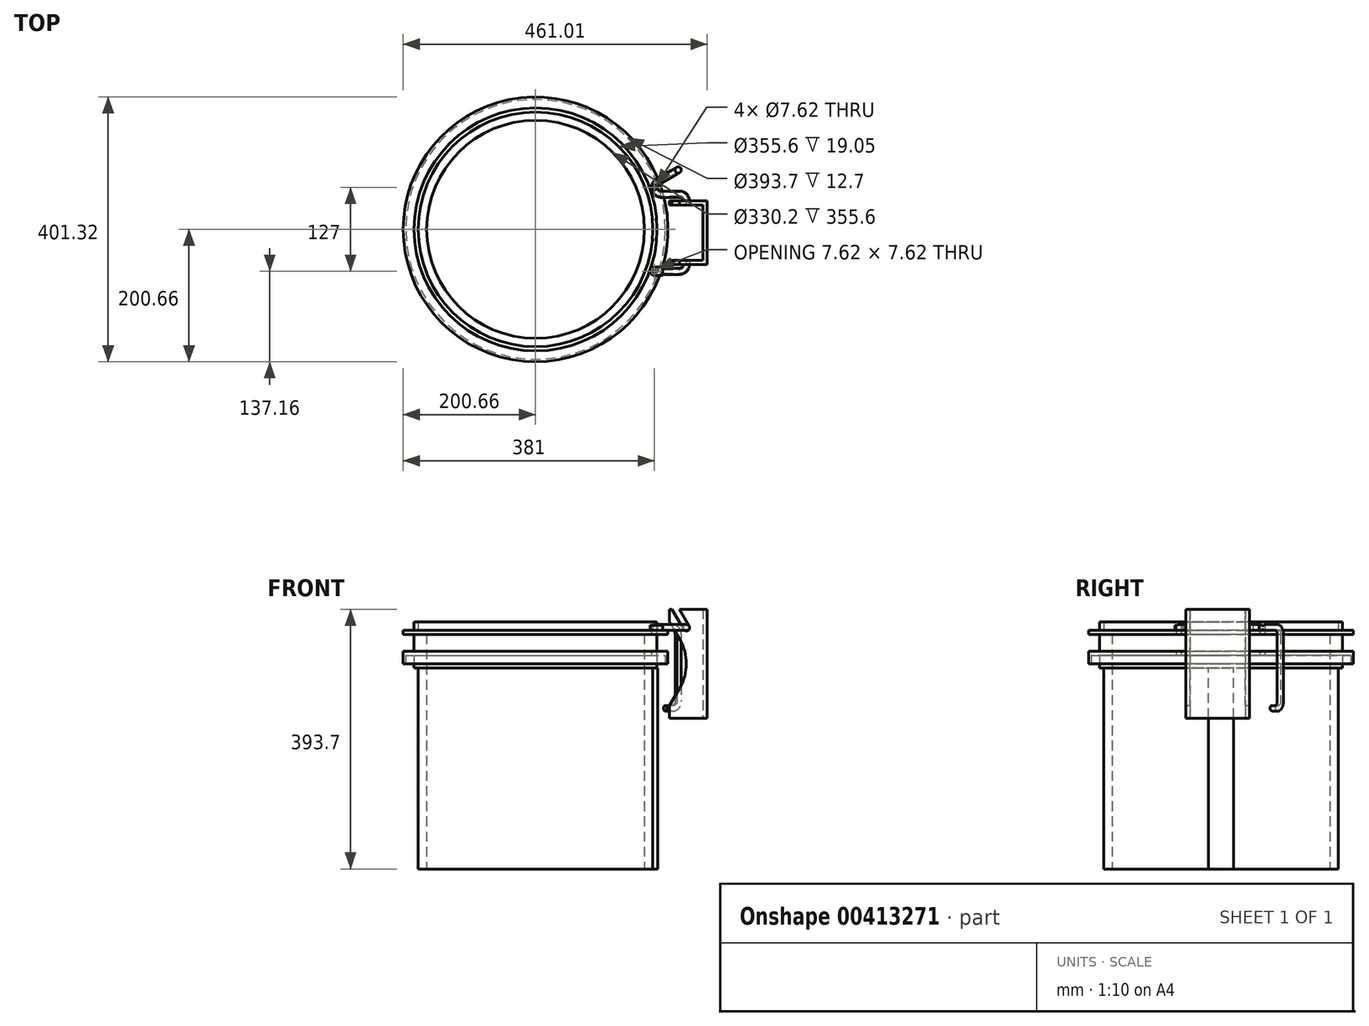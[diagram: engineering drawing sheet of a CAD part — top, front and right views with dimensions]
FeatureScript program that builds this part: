
annotation { "Feature Type Name" : "Feature", "Feature Type Description" : "" }
export const myFeature = defineFeature(function(context is Context, id is Id, definition is map)
    precondition{}
    {
        {
            var Q0;
            Q0=qCreatedBy(makeId("Front.planeOp"),FACE);
            var sketch = newSketch(context, id + "F0", { "sketchPlane" : qUnion([Q0])});
            skLineSegment(sketch, "E0", {"start": v(0, 0) * mm, "end": v(6.35, 0) * mm});
            skLineSegment(sketch, "E1", {"start": v(6.35, 0) * mm, "end": v(6.35, 19.05) * mm});
            skLineSegment(sketch, "E2", {"start": v(6.35, 19.05) * mm, "end": v(19.05, 19.05) * mm});
            skLineSegment(sketch, "E3", {"start": v(19.05, 19.05) * mm, "end": v(19.05, 6.35) * mm});
            skLineSegment(sketch, "E4", {"start": v(19.05, 6.35) * mm, "end": v(22.86, 6.35) * mm});
            skLineSegment(sketch, "E5", {"start": v(22.86, 6.35) * mm, "end": v(22.86, 25.4) * mm});
            skLineSegment(sketch, "E6", {"start": v(22.86, 25.4) * mm, "end": v(6.35, 25.4) * mm});
            skLineSegment(sketch, "E7", {"start": v(0, 25.4) * mm, "end": v(0, 0) * mm});
            skLineSegment(sketch, "E8", {"start": v(6.35, 25.4) * mm, "end": v(6.35, 50.8) * mm});
            skLineSegment(sketch, "E9", {"start": v(0, 50.8) * mm, "end": v(0, 25.4) * mm});
            skPoint(sketch, "E10", {"position": v(6.35, 25.4) * mm});
            skLineSegment(sketch, "E11", {"start": v(-177.8, 9.24) * mm, "end": v(-177.8, 50.6) * mm, "construction": true});
            skLineSegment(sketch, "E12", {"start": v(6.35, 50.8) * mm, "end": v(22.86, 50.8) * mm});
            skLineSegment(sketch, "E13", {"start": v(22.86, 50.8) * mm, "end": v(22.86, 57.15) * mm});
            skLineSegment(sketch, "E14", {"start": v(22.86, 57.15) * mm, "end": v(6.35, 57.15) * mm});
            skLineSegment(sketch, "E15", {"start": v(6.35, 57.15) * mm, "end": v(6.35, 69.85) * mm});
            skLineSegment(sketch, "E16", {"start": v(6.35, 69.85) * mm, "end": v(0, 69.85) * mm});
            skLineSegment(sketch, "E17", {"start": v(0, 69.85) * mm, "end": v(0, 50.8) * mm});
            skSolve(sketch);
        }
        {
            var Q0;
            Q0 = qSketchRegion(id + "F0", true);
            var Q1;
            Q1=sQuery(id+"F0.wireOp",EDGE,"E11");
            revolve(context, id + "F1", {"entities" : qUnion([Q0]), "axis" : qUnion([Q1]), "revolveType" : RevolveType.FULL});
        }
        {
            var Q0;
            Q0=makeQuery(id+"F1.opRevolve","SWEPT_FACE",FACE,{"disambiguationData":[OSD([sQuery(id+"F0.wireOp",EDGE,"E14")])]});
            var sketch = newSketch(context, id + "F2", { "sketchPlane" : qUnion([Q0])});
            skLineSegment(sketch, "E18", {"start": v(2.54, -87.99) * mm, "end": v(2.54, 87.99) * mm, "construction": true});
            skLineSegment(sketch, "E19", {"start": v(2.54, 0) * mm, "end": v(22.86, 0) * mm, "construction": true});
            skCircle(sketch, "E20", {"center": v(2.54, -63.5) * mm, "radius": 3.81 * mm});
            skCircle(sketch, "E21.MirrorC", {"center": v(2.54, 63.5) * mm, "radius": 3.81 * mm});
            skSolve(sketch);
        }
        {
            var Q0;
            Q0 = qSketchRegion(id + "F2", true);
            extrude(context, id + "F3", {"entities" : qUnion([Q0]), "operationType" : NewBodyOperationType.REMOVE, "endBound" : BoundingType.THROUGH_ALL, "oppositeDirection" : true, "depth" : 25.4 * mm});
        }
        {
            var Q0;
            Q0=makeQuery(id+"F1.opRevolve","SWEPT_FACE",FACE,{"disambiguationData":[OSD([sQuery(id+"F0.wireOp",EDGE,"E14")])]});
            var sketch = newSketch(context, id + "F4", { "sketchPlane" : qUnion([Q0])});
            skCircle(sketch, "E22", {"center": v(2.54, -63.5) * mm, "radius": 3.8 * mm});
            skLineSegment(sketch, "E23", {"start": v(2.54, -63.5) * mm, "end": v(27.94, -63.5) * mm, "construction": true});
            skLineSegment(sketch, "E24", {"start": v(15.24, -57.15) * mm, "end": v(2.54, -57.15) * mm});
            skPoint(sketch, "E24.startSnap0", {"position": v(15.24, -63.5) * mm});
            skLineSegment(sketch, "E25", {"start": v(2.54, -57.15) * mm, "end": v(2.54, -63.5) * mm, "construction": true});
            skArc(sketch, "E26", {"start": v(2.54, -57.15) * mm, "mid": v(-3.81, -63.5) * mm, "end": v(2.54, -69.85) * mm});
            skLineSegment(sketch, "E27", {"start": v(2.54, -69.85) * mm, "end": v(15.24, -69.85) * mm});
            skLineSegment(sketch, "E28", {"start": v(15.24, -69.85) * mm, "end": v(15.24, -57.15) * mm});
            skSolve(sketch);
        }
        {
            var Q0;
            Q0 = qSketchRegion(id + "F4", true);
            extrude(context, id + "F5", {"entities" : qUnion([Q0]), "depth" : 7.62 * mm});
        }
        {
            var Q0;
            Q0=makeQuery(id+"F5.opExtrude","SWEPT_FACE",FACE,{"disambiguationData":[OSD([sQuery(id+"F4.wireOp",EDGE,"E28")])]});
            var sketch = newSketch(context, id + "F6", { "sketchPlane" : qUnion([Q0])});
            skLineSegment(sketch, "E29", {"start": v(-69.85, 60.96) * mm, "end": v(-57.15, 60.96) * mm, "construction": true});
            skCircle(sketch, "E30", {"center": v(-63.5, 60.96) * mm, "radius": 4.76 * mm});
            skSolve(sketch);
        }
        {
            var Q0;
            Q0=sQuery(id+"F6.wireOp",EDGE,"E29");
            cPoint(context, id + "F7", {"entities" : qUnion([Q0]), "parameter" : 0.5});
        }
        {
            var Q0;
            Q0=qCreatedBy(makeId("Top.planeOp"),FACE);
            var Q1;
            Q1 = qCreatedBy(id + "F7" ,VERTEX);
            cPlane(context, id + "F8", {"entities" : qUnion([Q0, Q1]), "cplaneType" : CPlaneType.PLANE_POINT, "offset" : 25.4 * mm, "width" : 152.4 * mm, "height" : 152.4 * mm});
        }
        {
            var Q0;
            Q0=qCreatedBy(id+"F8.planeOp",FACE);
            var sketch = newSketch(context, id + "F9", { "sketchPlane" : qUnion([Q0])});
            skLineSegment(sketch, "E31", {"start": v(15.24, -63.5) * mm, "end": v(40.64, -63.5) * mm});
            skArc(sketch, "E32", {"start": v(40.64, -63.5) * mm, "mid": v(47.82, -60.52) * mm, "end": v(50.8, -53.34) * mm});
            skLineSegment(sketch, "E33", {"start": v(0, -5.08) * mm, "end": v(50.8, -5.08) * mm, "construction": true});
            skArc(sketch, "E34.MirrorCS", {"start": v(40.64, 53.34) * mm, "mid": v(47.82, 50.36) * mm, "end": v(50.8, 43.18) * mm});
            skPoint(sketch, "E35", {"position": v(2.54, 63.5) * mm});
            skLineSegment(sketch, "E36", {"start": v(40.64, 53.34) * mm, "end": v(12.7, 53.34) * mm});
            skArc(sketch, "E37", {"start": v(12.7, 53.34) * mm, "mid": v(5.52, 56.32) * mm, "end": v(2.54, 63.5) * mm});
            skLineSegment(sketch, "E38", {"start": v(2.54, 45.07) * mm, "end": v(2.54, 63.5) * mm, "construction": true});
            skArc(sketch, "E39", {"start": v(2.54, 63.5) * mm, "mid": v(3.9, 68.58) * mm, "end": v(7.62, 72.3) * mm});
            skLineSegment(sketch, "E40", {"start": v(7.62, 72.3) * mm, "end": v(29.62, 85) * mm});
            skLineSegment(sketch, "E41", {"start": v(50.8, -53.34) * mm, "end": v(50.8, 43.18) * mm});
            skSolve(sketch);
        }
        {
            var Q0;
            {var subQ0=sQuery(id+"F6.wireOp",EDGE,"E30");var subQ1=makeQuery(id+"F5.opExtrude","CAP_EDGE",EDGE,{"disambiguationData":[OSD([sQuery(id+"F4.wireOp",EDGE,"E28")])],"isStart":false});var subQ2=makeQuery(id+"F6.imprint","INTERSECT",VERTEX,{"disambiguationData":[OD(0.0)],"derivedFrom":[subQ1,subQ0]});Q0=makeQuery(id+"F6.imprint","IMPRINT",FACE,{"disambiguationData":[TD([[makeQuery(id+"F6.imprint","IMPRINT",EDGE,{"disambiguationData":[TD([[subQ2,1.0]])],"derivedFrom":subQ0}),1.0]])]});}
            var Q1;
            {var subQ0=sQuery(id+"F6.wireOp",EDGE,"E30");var subQ1=sQuery(id+"F4.wireOp",EDGE,"E28");var subQ2=makeQuery(id+"F5.opExtrude","CAP_EDGE",EDGE,{"disambiguationData":[OSD([subQ1])],"isStart":false});var subQ3=makeQuery(id+"F6.imprint","INTERSECT",VERTEX,{"disambiguationData":[OD(0.0)],"derivedFrom":[subQ2,subQ0]});Q1=makeQuery(id+"F6.imprint","IMPRINT",FACE,{"disambiguationData":[TD([[makeQuery(id+"F6.imprint","IMPRINT",EDGE,{"disambiguationData":[TD([[subQ3,-1.0]])],"derivedFrom":subQ0}),1.0]])]});}
            var Q2;
            {var subQ0=sQuery(id+"F6.wireOp",EDGE,"E30");var subQ1=makeQuery(id+"F5.opExtrude","CAP_EDGE",EDGE,{"disambiguationData":[OSD([sQuery(id+"F4.wireOp",EDGE,"E28")])],"isStart":true});var subQ2=makeQuery(id+"F6.imprint","INTERSECT",VERTEX,{"disambiguationData":[OD(0.0)],"derivedFrom":[subQ1,subQ0]});Q2=makeQuery(id+"F6.imprint","IMPRINT",FACE,{"disambiguationData":[TD([[makeQuery(id+"F6.imprint","IMPRINT",EDGE,{"disambiguationData":[TD([[subQ2,-1.0]])],"derivedFrom":subQ0}),1.0]])]});}
            var Q3;
            Q3=sQuery(id+"F9.wireOp",EDGE,"E31");
            var Q4;
            Q4=sQuery(id+"F9.wireOp",EDGE,"E32");
            var Q5;
            Q5=sQuery(id+"F9.wireOp",EDGE,"E41");
            var Q6;
            Q6=sQuery(id+"F9.wireOp",EDGE,"E34.MirrorCS");
            var Q7;
            Q7=sQuery(id+"F9.wireOp",EDGE,"E36");
            var Q8;
            Q8=sQuery(id+"F9.wireOp",EDGE,"E37");
            var Q9;
            Q9=sQuery(id+"F9.wireOp",EDGE,"E39");
            var Q10;
            Q10=sQuery(id+"F9.wireOp",EDGE,"E40");
            sweep(context, id + "F10", {"operationType" : NewBodyOperationType.ADD, "profiles" : qUnion([Q0, Q1, Q2]), "path" : qUnion([Q3, Q4, Q5, Q6, Q7, Q8, Q9, Q10])});
        }
        {
            var Q0;
            Q0=makeQuery(id+"F10.opSweep","CAP_FACE",FACE,{"disambiguationData":[OSD([sQuery(id+"F6.wireOp",EDGE,"E30"),sQuery(id+"F9.wireOp",VERTEX,"E40.end")])],"isStart":false});
            var sketch = newSketch(context, id + "F11", { "sketchPlane" : qUnion([Q0])});
            skCircle(sketch, "E42", {"center": v(58.8, 60.96) * mm, "radius": 4.73 * mm, "construction": true});
            skLineSegment(sketch, "E43", {"start": v(58.8, 60.96) * mm, "end": v(58.8, 65.72) * mm, "construction": true});
            skSolve(sketch);
        }
        {
            var Q0;
            Q0=sQuery(id+"F11.wireOp",VERTEX,"E43.end");
            var Q1;
            Q1=sQuery(id+"F11.wireOp",VERTEX,"E43.start");
            var Q2;
            Q2=sQuery(id+"F9.wireOp",VERTEX,"E40.start");
            cPlane(context, id + "F12", {"entities" : qUnion([Q0, Q1, Q2]), "cplaneType" : CPlaneType.THREE_POINT, "offset" : 25.4 * mm, "width" : 152.4 * mm, "height" : 152.4 * mm});
        }
        {
            var Q0;
            Q0=qCreatedBy(id+"F12.planeOp",FACE);
            var sketch = newSketch(context, id + "F13", { "sketchPlane" : qUnion([Q0])});
            skLineSegment(sketch, "E44", {"start": v(68.15, 60.96) * mm, "end": v(60.39, 60.96) * mm, "construction": true});
            skArc(sketch, "E45", {"start": v(68.15, 60.96) * mm, "mid": v(75.33, 57.98) * mm, "end": v(78.3, 50.8) * mm});
            skLineSegment(sketch, "E46", {"start": v(78.3, 50.8) * mm, "end": v(78.3, -50.8) * mm});
            skPoint(sketch, "E47.endSnap0", {"position": v(78.3, 0) * mm});
            skArc(sketch, "E48", {"start": v(78.3, -50.8) * mm, "mid": v(75.33, -57.98) * mm, "end": v(68.15, -60.96) * mm});
            skLineSegment(sketch, "E49", {"start": v(68.15, -60.96) * mm, "end": v(55.45, -60.96) * mm});
            skSolve(sketch);
        }
        {
            var Q0;
            Q0=makeQuery(id+"F11.imprint","IMPRINT",FACE,{"disambiguationData":[TD([[makeQuery(id+"F11.imprint","IMPRINT",EDGE,{"derivedFrom":makeQuery(id+"F10.opSweep","CAP_EDGE",EDGE,{"disambiguationData":[OSD([sQuery(id+"F6.wireOp",EDGE,"E30"),sQuery(id+"F9.wireOp",VERTEX,"E40.end")])],"isStart":false})}),1.0]])]});
            var Q1;
            Q1=sQuery(id+"F13.wireOp",EDGE,"E45");
            var Q2;
            Q2=sQuery(id+"F13.wireOp",EDGE,"E46");
            var Q3;
            Q3=sQuery(id+"F13.wireOp",EDGE,"E48");
            var Q4;
            Q4=sQuery(id+"F13.wireOp",EDGE,"E49");
            sweep(context, id + "F14", {"operationType" : NewBodyOperationType.ADD, "profiles" : qUnion([Q0]), "path" : qUnion([Q1, Q2, Q3, Q4])});
        }
        {
            var Q0;
            Q0=makeQuery(id+"F1.opRevolve","SWEPT_FACE",FACE,{"disambiguationData":[OSD([sQuery(id+"F0.wireOp",EDGE,"E14")])]});
            var sketch = newSketch(context, id + "F15", { "sketchPlane" : qUnion([Q0])});
            skCircle(sketch, "E50", {"center": v(2.54, 63.5) * mm, "radius": 3.81 * mm});
            skSolve(sketch);
        }
        {
            var Q0;
            Q0 = qSketchRegion(id + "F15", true);
            extrude(context, id + "F16", {"entities" : qUnion([Q0]), "operationType" : NewBodyOperationType.REMOVE, "endBound" : BoundingType.THROUGH_ALL, "oppositeDirection" : true, "depth" : 25.4 * mm, "hasSecondDirection" : true, "secondDirectionBound" : SecondDirectionBoundingType.THROUGH_ALL, "secondDirectionOppositeDirection" : false, "secondDirectionDepth" : 25.4 * mm});
        }
        {
            var Q0;
            Q0=qCreatedBy(makeId("Front.planeOp"),FACE);
            var sketch = newSketch(context, id + "F17", { "sketchPlane" : qUnion([Q0])});
            skLineSegment(sketch, "E51", {"start": v(0, 0) * mm, "end": v(0, -304.8) * mm});
            skLineSegment(sketch, "E52", {"start": v(0, 0) * mm, "end": v(0, 50.8) * mm});
            skLineSegment(sketch, "E53", {"start": v(0, 50.8) * mm, "end": v(-12.7, 50.8) * mm});
            skLineSegment(sketch, "E54", {"start": v(-12.7, 50.8) * mm, "end": v(-12.7, -304.8) * mm});
            skLineSegment(sketch, "E55", {"start": v(-12.7, -304.8) * mm, "end": v(0, -304.8) * mm});
            skSolve(sketch);
        }
        {
            var Q0;
            Q0 = qSketchRegion(id + "F17", true);
            var Q1;
            Q1=makeQuery(id+"F1.opRevolve","SWEPT_FACE",FACE,{"disambiguationData":[OSD([sQuery(id+"F0.wireOp",EDGE,"E7"),sQuery(id+"F0.wireOp",EDGE,"E9"),sQuery(id+"F0.wireOp",EDGE,"E17")])]});
            revolve(context, id + "F18", {"operationType" : NewBodyOperationType.ADD, "entities" : qUnion([Q0]), "axis" : qUnion([Q1]), "revolveType" : RevolveType.FULL});
        }
        {
            var Q0;
            Q0=makeQuery(id+"F1.opRevolve","SWEPT_FACE",FACE,{"disambiguationData":[OSD([sQuery(id+"F0.wireOp",EDGE,"E0")])]});
            var sketch = newSketch(context, id + "F19", { "sketchPlane" : qUnion([Q0])});
            skLineSegment(sketch, "E56", {"start": v(0, 0) * mm, "end": v(0, 19.05) * mm});
            skLineSegment(sketch, "E57", {"start": v(0, 0) * mm, "end": v(0, -19.05) * mm});
            skArc(sketch, "E58", {"start": v(0, -19.05) * mm, "mid": v(7.62, 0) * mm, "end": v(0, 19.05) * mm});
            skSolve(sketch);
        }
        {
            var Q0;
            Q0 = qSketchRegion(id + "F19", true);
            var Q1;
            Q1=makeQuery(id+"F18.opRevolve","SWEPT_FACE",FACE,{"disambiguationData":[OSD([sQuery(id+"F17.wireOp",EDGE,"E55")])]});
            extrude(context, id + "F20", {"entities" : qUnion([Q0]), "endBound" : BoundingType.UP_TO_SURFACE, "endBoundEntityFace" : qUnion([Q1]), "depth" : 25.4 * mm});
        }
        {
            var Q0;
            Q0=qCreatedBy(makeId("Top.planeOp"),FACE);
            var sketch = newSketch(context, id + "F21", { "sketchPlane" : qUnion([Q0])});
            skLineSegment(sketch, "E59", {"start": v(39.24, 43.18) * mm, "end": v(39.24, -53.34) * mm, "construction": true});
            skLineSegment(sketch, "E60", {"start": v(39.24, -5.08) * mm, "end": v(82.55, -5.08) * mm, "construction": true});
            skLineSegment(sketch, "E61", {"start": v(82.55, -5.08) * mm, "end": v(82.55, 43.18) * mm});
            skLineSegment(sketch, "E62", {"start": v(82.55, 43.18) * mm, "end": v(25.4, 43.18) * mm});
            skLineSegment(sketch, "E63.0", {"start": v(76.2, 36.83) * mm, "end": v(25.4, 36.83) * mm});
            skLineSegment(sketch, "E63.1", {"start": v(76.2, -5.08) * mm, "end": v(76.2, 36.83) * mm});
            skLineSegment(sketch, "E64", {"start": v(25.4, 43.18) * mm, "end": v(25.4, 36.83) * mm});
            skLineSegment(sketch, "E65.MirrorCS", {"start": v(25.4, -53.34) * mm, "end": v(25.4, -47) * mm});
            skLineSegment(sketch, "E66.MirrorCS", {"start": v(76.2, -5.08) * mm, "end": v(76.2, -47) * mm});
            skLineSegment(sketch, "E67.MirrorCS", {"start": v(82.55, -5.08) * mm, "end": v(82.55, -53.34) * mm});
            skLineSegment(sketch, "E68.MirrorCS", {"start": v(76.2, -47) * mm, "end": v(25.4, -47) * mm});
            skLineSegment(sketch, "E69.MirrorCS", {"start": v(82.55, -53.34) * mm, "end": v(25.4, -53.34) * mm});
            skSolve(sketch);
        }
        {
            var Q0;
            Q0 = qSketchRegion(id + "F21", true);
            extrude(context, id + "F22", {"entities" : qUnion([Q0]), "depth" : 88.9 * mm, "hasSecondDirection" : true, "secondDirectionOppositeDirection" : true, "secondDirectionDepth" : 76.2 * mm});
        }
        {
            var Q0;
            Q0=makeQuery(id+"F22.opExtrude","SWEPT_FACE",FACE,{"disambiguationData":[OSD([sQuery(id+"F21.wireOp",EDGE,"E69.MirrorCS")])]});
            var sketch = newSketch(context, id + "F23", { "sketchPlane" : qUnion([Q0])});
            skCircle(sketch, "E70", {"center": v(50.8, 60.96) * mm, "radius": 5.08 * mm});
            skLineSegment(sketch, "E71", {"start": v(50.8, 60.96) * mm, "end": v(34.67, 88.9) * mm, "construction": true});
            skLineSegment(sketch, "E72", {"start": v(50.8, 60.96) * mm, "end": v(50.8, 88.9) * mm, "construction": true});
            skLineSegment(sketch, "E73", {"start": v(46.4, 58.42) * mm, "end": v(28.8, 88.9) * mm});
            skLineSegment(sketch, "E74", {"start": v(55.2, 63.5) * mm, "end": v(40.53, 88.9) * mm});
            skLineSegment(sketch, "E75", {"start": v(28.8, 88.9) * mm, "end": v(40.53, 88.9) * mm});
            skLineSegment(sketch, "E76", {"start": v(25.4, 69.85) * mm, "end": v(41.05, 42.75) * mm});
            skLineSegment(sketch, "E77", {"start": v(25.4, 6.35) * mm, "end": v(76.2, 6.35) * mm, "construction": true});
            skPoint(sketch, "E77.endSnap0", {"position": v(82.55, 6.35) * mm});
            skArc(sketch, "E78", {"start": v(41.05, 42.75) * mm, "mid": v(48.32, 25.2) * mm, "end": v(50.8, 6.35) * mm});
            skLineSegment(sketch, "E79", {"start": v(50.8, -16.5) * mm, "end": v(50.8, 6.35) * mm, "construction": true});
            skArc(sketch, "E80.MirrorCS", {"start": v(41.05, -30.05) * mm, "mid": v(48.32, -12.5) * mm, "end": v(50.8, 6.35) * mm});
            skLineSegment(sketch, "E81.MirrorCS", {"start": v(25.4, -57.15) * mm, "end": v(41.05, -30.05) * mm});
            skLineSegment(sketch, "E82", {"start": v(25.4, 69.85) * mm, "end": v(25.4, -57.15) * mm});
            skSolve(sketch);
        }
        {
            var Q0;
            Q0 = qSketchRegion(id + "F23", true);
            var Q1;
            Q1=makeQuery(id+"F22.opExtrude","SWEPT_FACE",FACE,{"disambiguationData":[OSD([sQuery(id+"F21.wireOp",EDGE,"E62")])]});
            extrude(context, id + "F24", {"entities" : qUnion([Q0]), "operationType" : NewBodyOperationType.REMOVE, "endBound" : BoundingType.UP_TO_SURFACE, "oppositeDirection" : true, "endBoundEntityFace" : qUnion([Q1]), "depth" : 25.4 * mm});
        }
    });
